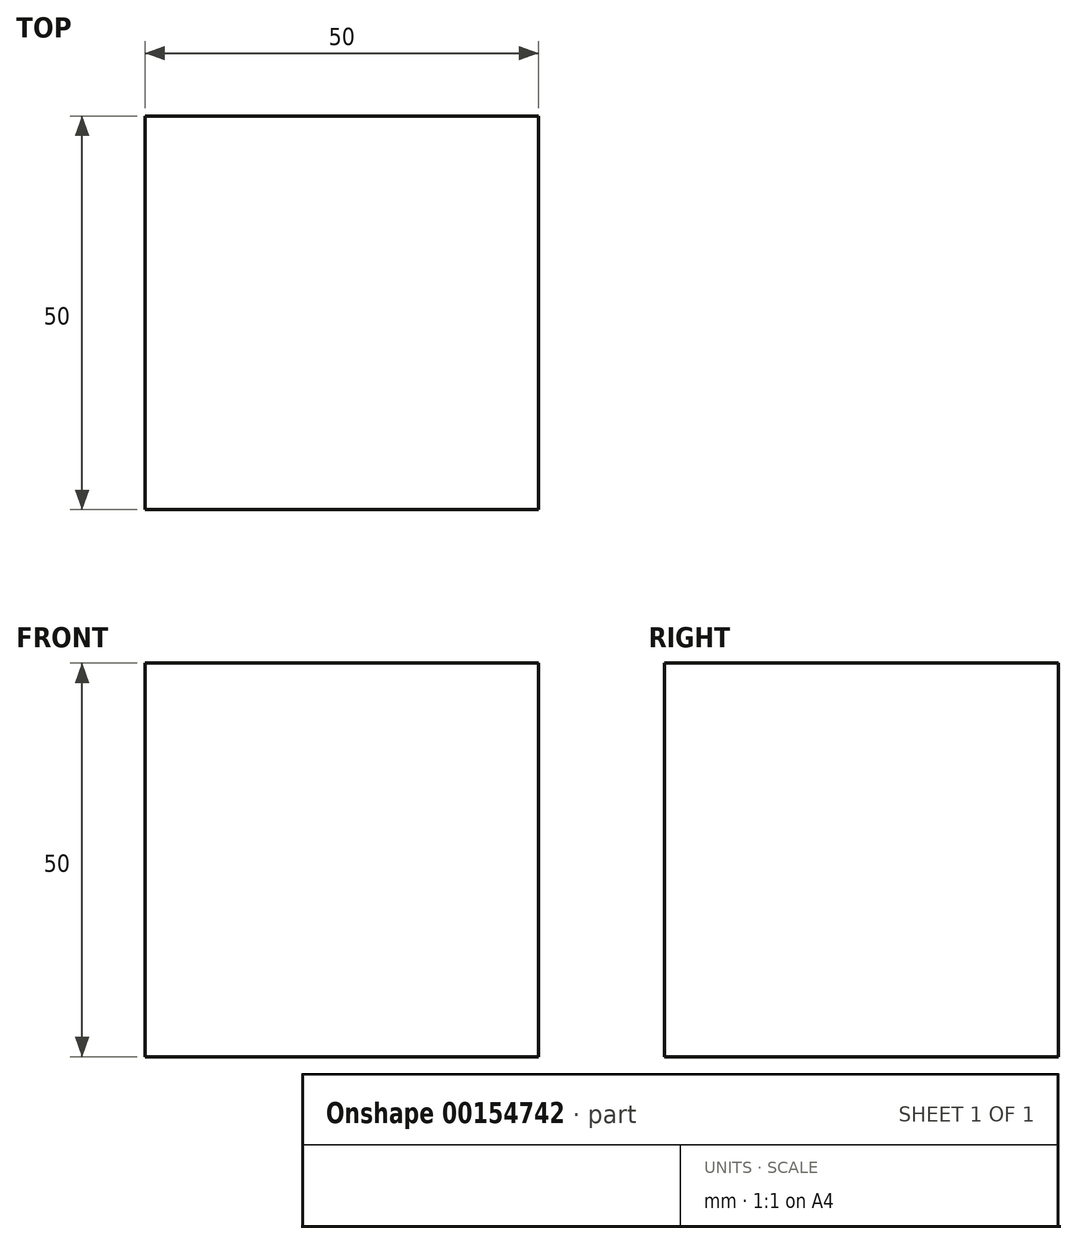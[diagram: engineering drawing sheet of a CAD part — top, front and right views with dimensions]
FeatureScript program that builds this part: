
annotation { "Feature Type Name" : "Feature", "Feature Type Description" : "" }
export const myFeature = defineFeature(function(context is Context, id is Id, definition is map)
    precondition{}
    {
        {
            var Q0;
            Q0=qCreatedBy(makeId("Top.planeOp"),FACE);
            var sketch = newSketch(context, id + "F0", { "sketchPlane" : qUnion([Q0])});
            skLineSegment(sketch, "E0.bottom", {"start": v(25, 25) * mm, "end": v(-25, 25) * mm});
            skLineSegment(sketch, "E0.top", {"start": v(25, -25) * mm, "end": v(-25, -25) * mm});
            skLineSegment(sketch, "E0.left", {"start": v(25, 25) * mm, "end": v(25, -25) * mm});
            skLineSegment(sketch, "E0.right", {"start": v(-25, 25) * mm, "end": v(-25, -25) * mm});
            skPoint(sketch, "E0.middle", {"position": v(0, 0) * mm});
            skSolve(sketch);
        }
        {
            var Q0;
            Q0=makeQuery(id+"F0.imprint","IMPRINT",FACE,{"disambiguationData":[TD([[makeQuery(id+"F0.imprint","IMPRINT",EDGE,{"derivedFrom":sQuery(id+"F0.wireOp",EDGE,"E0.bottom")}),1.0]])]});
            extrude(context, id + "F1", {"entities" : qUnion([Q0]), "endBound" : BoundingType.SYMMETRIC, "depth" : 50 * mm});
        }
    });
